# Revit family: Hager-Volta-IP30-Surface_mounted-syst-AT-de
name_source: partatom
category: Electrical Equipment
units: mm (PartAtom-declared; Revit-internal decimal feet)

## family parameters
Cut with Voids When Loaded = No
Host = Face
Panel Configuration = Two Columns, Circuits Across
Part Type = Panelboard
Room Calculation Point = No
Round Connector Dimension = Use Diameter
Shared = No

## types (4) — shared parameters
EF000003 - Montageart = EV000384 - Aufputz
EF000008 - Breite = 305 mm  [stored 1.00066 ft]
EF000049 - Tiefe = 96 mm  [stored 0.314961 ft]
EF000116 - RAL-Nummer = 9010
EF000118 - Mit Montageplatte = No
EF000339 - Art der Abdeckung = EV000494 - ohne
EF001062 - EMV-Ausführung = No
EF001088 - Anbaumöglichkeit = Yes
EF001134 - DIN-Schiene = No
EF002950 - Breite in Teilungseinheiten = 12
EF005474 - Schutzart (IP) = EV006410 - IP30
EF006244 - Transparenter Deckel/Tür = No
EF006306 - Mit Schloss = No
EF009212 - Ausführung Deckel = EV009916 - mit Ausschnitt
EF015776 - Erdungsklemmenblock = No
EF015777 - Neutralleiterklemmenblock = No
EF015941 - Signaldurchlassende Tür = No
HG000001 - Anzahl der Spalten = 1
HG000002 - Mit tür = No
HG000003 - Bereich = Volta
HG000005 - Dicke = 3 mm  [stored 0.00984252 ft]
HG000006 - Unterputz = No
HG000009 - Doppelflügeligen Tür = No
HG000010 - Asymmetrische Türen = No
HG000011 - Leere Reihen von unten = No
HG000017 - Distanz zwischen den Polen = 18 mm  [stored 0.0590551 ft]
Manufacturer = Hager
Type Comments = Volta
zero-valued in all types: Default Elevation, EF000218 - Einbautiefe, EF000332 - Einbauhöhe, EF000846 - Einbaubreite, EF001131 - Innentiefe, HG000007 - Anzahl der leeren Spalten, HG000008 - Anzahl der leeren Reihen

## per-type parameters (varying)
| type | EF000040 - Höhe | EF000266 - Anzahl der Reihen | HG000004 - Herstellerreferenz | Model |
| Aufputz IP30 B305 H245 T96.5 12 Teilungseinheiten - VA12BN | 245 mm | 1 | VA12BN | VA12BN |
| Aufputz IP30 B305 H370 T96.5 12 Teilungseinheiten - VA24BN | 370 mm | 2 | VA24BN | VA24BN |
| Aufputz IP30 B305 H515 T96.5 12 Teilungseinheiten - VA36BN | 515 mm | 3 | VA36BN | VA36BN |
| Aufputz IP30 B305 H640 T96.5 12 Teilungseinheiten - VA48BN | 640 mm  [stored 2.09974 ft] | 4 | VA48BN | VA48BN |

note: [stored X ft] marks values corroborated as IEEE doubles in the binary element streams (Revit-internal decimal feet)

## geometry (parser evidence)
native form markers: Sweep x17
no freeform markers — native parametric forms only
